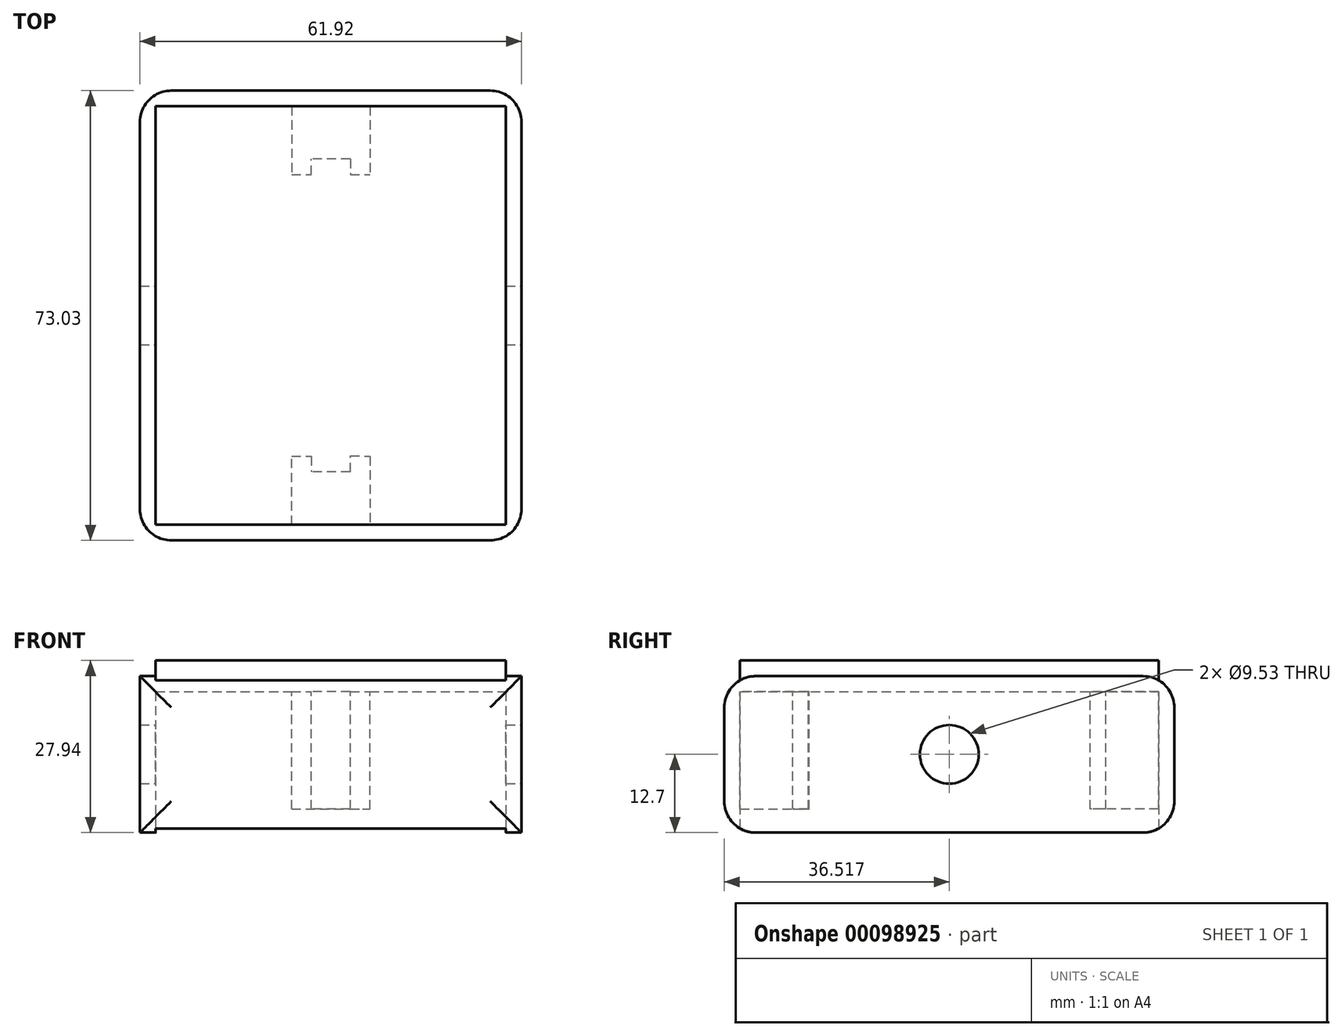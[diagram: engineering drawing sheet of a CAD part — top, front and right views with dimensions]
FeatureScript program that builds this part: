
annotation { "Feature Type Name" : "Feature", "Feature Type Description" : "" }
export const myFeature = defineFeature(function(context is Context, id is Id, definition is map)
    precondition{}
    {
        {
            var Q0;
            Q0=qCreatedBy(makeId("Front.planeOp"),FACE);
            var sketch = newSketch(context, id + "F0", { "sketchPlane" : qUnion([Q0])});
            skLineSegment(sketch, "E0.bottom", {"start": v(-30.96, 12.7) * mm, "end": v(30.96, 12.7) * mm});
            skLineSegment(sketch, "E0.top", {"start": v(-30.96, -12.7) * mm, "end": v(30.96, -12.7) * mm});
            skLineSegment(sketch, "E0.left", {"start": v(-30.96, 12.7) * mm, "end": v(-30.96, -12.7) * mm});
            skLineSegment(sketch, "E0.right", {"start": v(30.96, 12.7) * mm, "end": v(30.96, -12.7) * mm});
            skPoint(sketch, "E0.middle", {"position": v(0, 0) * mm});
            skSolve(sketch);
        }
        {
            var Q0;
            Q0=makeQuery(id+"F0.imprint","IMPRINT",FACE,{"disambiguationData":[TD([[makeQuery(id+"F0.imprint","IMPRINT",EDGE,{"derivedFrom":sQuery(id+"F0.wireOp",EDGE,"E0.bottom")}),-1.0]])]});
            extrude(context, id + "F1", {"entities" : qUnion([Q0]), "depth" : 73.02 * mm});
        }
        {
            var Q0;
            Q0=makeQuery(id+"F1.opExtrude","SWEPT_FACE",FACE,{"disambiguationData":[OSD([sQuery(id+"F0.wireOp",EDGE,"E0.right")])]});
            var sketch = newSketch(context, id + "F2", { "sketchPlane" : qUnion([Q0])});
            skPoint(sketch, "E1.endSnap0", {"position": v(-36.51, 12.7) * mm});
            skCircle(sketch, "E2", {"center": v(-36.51, 0) * mm, "radius": 4.76 * mm});
            skSolve(sketch);
        }
        {
            var Q0;
            Q0=makeQuery(id+"F1.opExtrude","SWEPT_FACE",FACE,{"disambiguationData":[OSD([sQuery(id+"F0.wireOp",EDGE,"E0.top")])]});
            shell(context, id + "F3", {"entities" : qUnion([Q0]), "thickness" : 2.54 * mm});
        }
        {
            var Q0;
            Q0=makeQuery(id+"F1.opExtrude","SWEPT_FACE",FACE,{"disambiguationData":[OSD([sQuery(id+"F0.wireOp",EDGE,"E0.bottom")])]});
            var sketch = newSketch(context, id + "F4", { "sketchPlane" : qUnion([Q0])});
            skLineSegment(sketch, "E3.bottom", {"start": v(28.42, -2.54) * mm, "end": v(-28.42, -2.54) * mm});
            skLineSegment(sketch, "E3.top", {"start": v(28.42, -70.48) * mm, "end": v(-28.42, -70.48) * mm});
            skLineSegment(sketch, "E3.left", {"start": v(28.42, -2.54) * mm, "end": v(28.42, -70.48) * mm});
            skLineSegment(sketch, "E3.right", {"start": v(-28.42, -2.54) * mm, "end": v(-28.42, -70.48) * mm});
            skPoint(sketch, "E3.middle", {"position": v(0, -36.51) * mm});
            skPoint(sketch, "E3.middle.positionSnap0", {"position": v(-30.96, -36.51) * mm});
            skPoint(sketch, "E3.centerSnap0", {"position": v(-30.96, -36.51) * mm});
            skSolve(sketch);
        }
        {
            var Q0;
            Q0=qSketchRegion(id+"F4",true);
            extrude(context, id + "F5", {"entities" : qUnion([Q0]), "operationType" : NewBodyOperationType.ADD, "depth" : 2.54 * mm});
        }
        {
            var Q0;
            Q0=makeQuery(id+"F1.opExtrude","CAP_FACE",FACE,{"disambiguationData":[OSD([sQuery(id+"F0.wireOp",EDGE,"E0.bottom"),sQuery(id+"F0.wireOp",EDGE,"E0.top"),sQuery(id+"F0.wireOp",EDGE,"E0.left"),sQuery(id+"F0.wireOp",EDGE,"E0.right")])],"isStart":true});
            fillet(context, id + "F6", {"entities" : qUnion([Q0]), "radius" : 5.08 * mm, "tangentPropagation" : true, "allowEdgeOverflow" : false});
        }
        {
            var Q0;
            Q0=makeQuery(id+"F1.opExtrude","CAP_FACE",FACE,{"disambiguationData":[OSD([sQuery(id+"F0.wireOp",EDGE,"E0.bottom"),sQuery(id+"F0.wireOp",EDGE,"E0.top"),sQuery(id+"F0.wireOp",EDGE,"E0.left"),sQuery(id+"F0.wireOp",EDGE,"E0.right")])],"isStart":false});
            fillet(context, id + "F7", {"entities" : qUnion([Q0]), "radius" : 5.08 * mm, "tangentPropagation" : true, "allowEdgeOverflow" : false});
        }
        {
            var Q0;
            Q0=makeQuery(id+"F2.imprint","IMPRINT",FACE,{"disambiguationData":[TD([[makeQuery(id+"F2.imprint","IMPRINT",EDGE,{"derivedFrom":sQuery(id+"F2.wireOp",EDGE,"E2")}),1.0]])]});
            var Q1;
            Q1=sQuery(id+"F2.wireOp",EDGE,"E2");
            extrude(context, id + "F8", {"entities" : qUnion([Q0]), "operationType" : NewBodyOperationType.REMOVE, "surfaceEntities" : qUnion([Q1]), "endBound" : BoundingType.THROUGH_ALL, "oppositeDirection" : true, "depth" : 25.4 * mm});
        }
        {
            var Q0;
            Q0=makeQuery(id+"F3.opShell","OFFSET_FACE",FACE,{"disambiguationData":[OSD([sQuery(id+"F0.wireOp",EDGE,"E0.bottom")])]});
            var sketch = newSketch(context, id + "F9", { "sketchPlane" : qUnion([Q0])});
            skLineSegment(sketch, "E4.bottom", {"start": v(3.18, 61.91) * mm, "end": v(-3.17, 61.91) * mm});
            skLineSegment(sketch, "E4.top", {"start": v(3.18, 11.11) * mm, "end": v(-3.17, 11.11) * mm});
            skPoint(sketch, "E4.middle", {"position": v(0, 36.51) * mm});
            skPoint(sketch, "E4.middle.positionSnap0", {"position": v(-28.42, 36.51) * mm});
            skPoint(sketch, "E4.centerSnap0", {"position": v(-28.42, 36.51) * mm});
            skLineSegment(sketch, "E5", {"start": v(0, 70.48) * mm, "end": v(-6.35, 70.48) * mm});
            skLineSegment(sketch, "E6", {"start": v(-6.35, 70.48) * mm, "end": v(-6.35, 61.91) * mm});
            skLineSegment(sketch, "E7", {"start": v(0, 70.48) * mm, "end": v(6.35, 70.48) * mm});
            skLineSegment(sketch, "E8", {"start": v(6.35, 70.48) * mm, "end": v(6.35, 61.91) * mm});
            skLineSegment(sketch, "E9", {"start": v(-6.35, 61.91) * mm, "end": v(-6.35, 59.37) * mm});
            skLineSegment(sketch, "E10", {"start": v(6.35, 59.37) * mm, "end": v(6.35, 61.91) * mm});
            skLineSegment(sketch, "E11", {"start": v(-6.35, 59.37) * mm, "end": v(-3.17, 59.37) * mm});
            skLineSegment(sketch, "E12", {"start": v(-3.17, 59.37) * mm, "end": v(-3.17, 61.91) * mm});
            skLineSegment(sketch, "E13", {"start": v(3.18, 61.91) * mm, "end": v(3.18, 59.28) * mm});
            skLineSegment(sketch, "E14", {"start": v(3.18, 59.28) * mm, "end": v(6.35, 59.37) * mm});
            skLineSegment(sketch, "E15", {"start": v(-6.35, 2.54) * mm, "end": v(6.35, 2.54) * mm});
            skLineSegment(sketch, "E16", {"start": v(6.35, 2.54) * mm, "end": v(6.35, 11.11) * mm});
            skLineSegment(sketch, "E17", {"start": v(-6.35, 2.54) * mm, "end": v(-6.35, 11.11) * mm});
            skLineSegment(sketch, "E18", {"start": v(-6.35, 11.11) * mm, "end": v(-6.35, 13.65) * mm});
            skLineSegment(sketch, "E19", {"start": v(-6.35, 13.65) * mm, "end": v(-3.17, 13.65) * mm});
            skLineSegment(sketch, "E20", {"start": v(-3.17, 13.65) * mm, "end": v(-3.17, 11.11) * mm});
            skLineSegment(sketch, "E21", {"start": v(3.18, 11.11) * mm, "end": v(3.18, 13.65) * mm});
            skLineSegment(sketch, "E22", {"start": v(3.18, 13.65) * mm, "end": v(6.35, 13.65) * mm});
            skLineSegment(sketch, "E23", {"start": v(6.35, 13.65) * mm, "end": v(6.35, 11.11) * mm});
            skSolve(sketch);
        }
        {
            var Q0;
            Q0=qSketchRegion(id+"F9",true);
            extrude(context, id + "F10", {"entities" : qUnion([Q0]), "operationType" : NewBodyOperationType.ADD, "depth" : 19.05 * mm});
        }
    });
